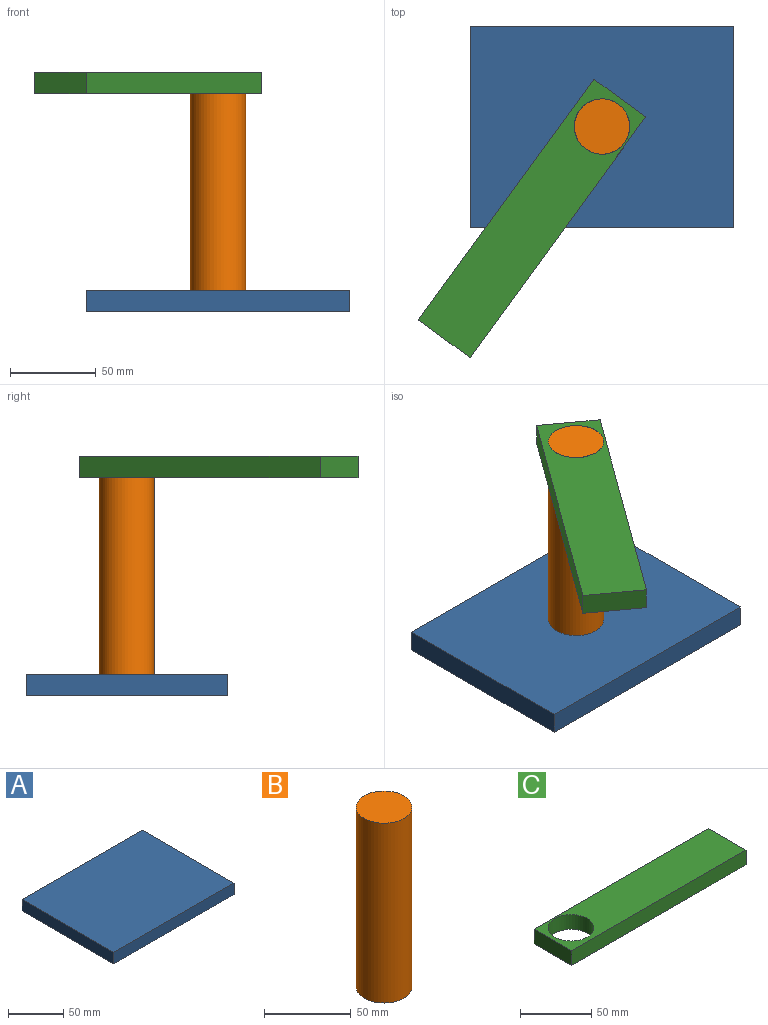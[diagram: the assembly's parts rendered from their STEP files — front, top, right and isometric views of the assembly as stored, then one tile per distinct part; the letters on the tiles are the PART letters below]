
ASSEMBLY  parts=3 mates=2
PART A: 6 faces, bbox 153.4x117.4x12.7 mm
  f0: plane 153.35x12.7mm, normal (0,-1,0), area 1947.6mm2, adj f1,f3,f4,f5
  f1: plane 117.37x12.7mm, normal (1,0,0), area 1490.6mm2, adj f0,f2,f4,f5
  f2: plane 153.35x12.7mm, normal (0,1,0), area 1947.6mm2, adj f1,f3,f4,f5
  f3: plane 117.37x12.7mm, normal (-1,0,0), area 1490.6mm2, adj f0,f2,f4,f5
  f4: plane 153.35x117.37mm, normal (0,0,1), area 17999mm2, adj f0,f1,f2,f3
  f5: plane 153.35x117.37mm, normal (0,0,-1), area 17999mm2, adj f0,f1,f2,f3
PART B: 3 faces, bbox 32.2x32.2x127 mm
  f0: cylinder r=16.12mm len=127mm, axis (0,0,-1), area 12861mm2, adj f1,f2
  f1: plane 32.23x32.23mm, normal (0,0,1), area 816.1mm2, adj f0
  f2: plane 32.23x32.23mm, normal (0,0,-1), area 816.1mm2, adj f0
PART C: 7 faces, bbox 173.6x37.4x12.7 mm
  f0: plane 37.41x12.7mm, normal (-1,0,0), area 475.1mm2, adj f1,f4,f5,f6
  f1: plane 173.63x12.7mm, normal (0,-1,0), area 2205.1mm2, adj f0,f2,f5,f6
  f2: plane 37.41x12.7mm, normal (1,0,0), area 475.1mm2, adj f1,f4,f5,f6
  f3: cylinder r=16.12mm len=32.23mm, axis (0,0,-1), area 1286.1mm2, adj f5,f6
  f4: plane 173.63x12.7mm, normal (0,1,0), area 2205.1mm2, adj f0,f2,f5,f6
  f5: plane 173.63x37.41mm, normal (0,0,1), area 5679.4mm2, adj f0,f1,f2,f3,f4
  f6: plane 173.63x37.41mm, normal (0,0,-1), area 5679.4mm2, adj f0,f1,f2,f3,f4
PLACE A t=(-22.36,35.23,-37.51)mm fixed
PLACE B t=(-22.36,35.23,-37.51)mm
PLACE C rot(axis=(0,0,-1),126.1deg) t=(-22.36,35.23,-50.21)mm
MATE revolute B.f0 <-> C.f3  axis (0,0,1) through (-22.36,35.23,102.19)mm
MATE fastened A.f4 <-> B.f0  axis (0,0,1) through (-22.36,35.23,-24.81)mm
